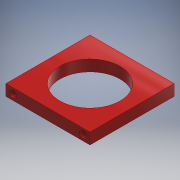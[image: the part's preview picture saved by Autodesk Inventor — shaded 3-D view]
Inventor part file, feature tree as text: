
AUTODESK INVENTOR PART (.ipt)
format: ipt  version: 2019.3 (Build 233278000, 278)  size: 116,736 bytes
history: native  units: mm
features: sketch x2, hole x2, extrude x1, projected_geometry x1
ambient origin geometry x8: Origin, YZ Plane, XZ Plane, XY Plane, X Axis, Y Axis, Z Axis, Center Point
bodies: Solid1 (feature_tree)
feature tree (6):
  sketch  "Sketch1"  dims[d0=60.0mm d1=60.0mm]
  extrude  "Extrusion1"  Depth=60.0mm
  hole  "Hole1"  [1 undecoded]
  hole  "Hole2"  [1 undecoded]
  sketch  "Sketch2"  dims[d2=8.0mm d3=0.0mm d4=43.0mm d5=6.0mm d6=4.0mm d7=2.0mm d8=90.0deg d9=8.0mm d10=20.594885mm d11=5.0mm d12=5.0mm d13=5.0mm d14=6.0mm d15=4.0mm d16=2.0mm d17=90.0deg d18=8.0mm d19=20.594885mm]
  projected_geometry  "Projected Loop1"
note: 2 required parameter values undecoded (feature->parameter linkage not recoverable at this tier; creation-order binding heuristic only, values carry confidence <= 0.55)
